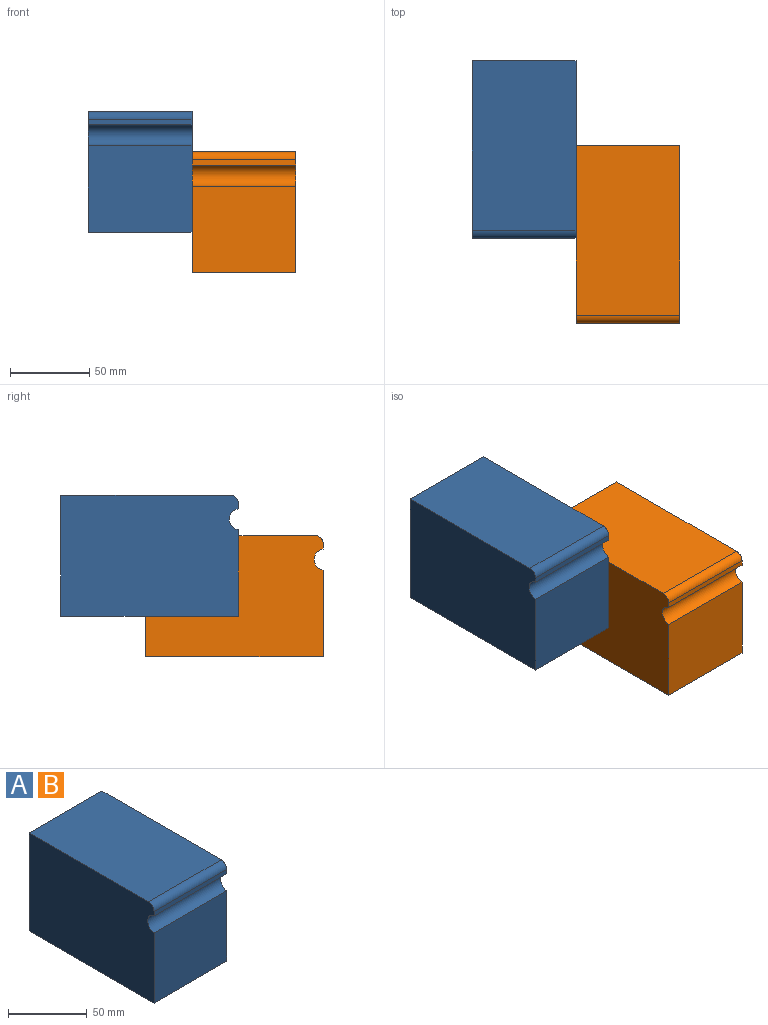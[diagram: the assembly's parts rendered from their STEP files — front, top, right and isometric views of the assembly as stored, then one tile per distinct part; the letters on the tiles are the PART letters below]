
ASSEMBLY  parts=2 mates=1
PART A: 9 faces, bbox 65.3x112x76.2 mm
  f0: plane 65.3x3.38mm, normal (0,-1,0), area 220.4mm2, adj f5,f6,f7,f8
  f1: plane 107x65.3mm, normal (0,0,1), area 6987.1mm2, adj f4,f5,f6,f8
  f2: plane 65.3x54.58mm, normal (0,-1,0), area 3563.8mm2, adj f3,f5,f6,f7
  f3: plane 112x65.3mm, normal (0,0,-1), area 7313.6mm2, adj f2,f4,f5,f6
  f4: plane 76.2x65.3mm, normal (0,1,0), area 4975.9mm2, adj f1,f3,f5,f6
  f5: plane 112x76.2mm, normal (1,0,0), area 8471.9mm2, adj f0,f1,f2,f3,f4,f7,f8
  f6: plane 112x76.2mm, normal (-1,0,0), area 8471.9mm2, adj f0,f1,f2,f3,f4,f7,f8
  f7: cylinder r=6.7mm len=65.3mm, axis (1,0,0), area 1243.4mm2, adj f0,f2,f5,f6
  f8: cylinder r=5mm len=65.3mm, axis (1,0,0), area 512.9mm2, adj f0,f1,f5,f6
PART B: same geometry as A
PLACE A t=(41.08,86.66,-40.36)mm
PLACE B t=(106.38,33.16,-65.76)mm
MATE planar B.f6 <-> A.f5  axis (-1,0,0) through (106.38,48.81,-93.07)mm
